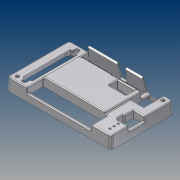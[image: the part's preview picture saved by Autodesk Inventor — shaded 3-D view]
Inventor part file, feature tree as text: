
AUTODESK INVENTOR PART (.ipt)
format: ipt  version: unknown  size: 2,817,024 bytes
history: native  units: mm (DEFAULTED — no unit token found)
features: extrude x22, sketch x13, fillet x7, plane x7, other x6, projected_geometry x1
ambient origin geometry x5: Origin, X Axis, Y Axis, Z Axis, Center Point
feature tree (56):
  other  "Basic Profile Sketch"
  extrude  "Above PCB Extrusion"  Depth=71.12mm
  extrude  "Below Extrusion"  Depth=10.16mm
  extrude  "Board Level Edge Cuts"  Depth=2.032mm
  extrude  "Board Level Supports"  Depth=48.1076mm
  extrude  "LED Viewing Angle Increase"  Depth=8.382mm
  other  "DB Sketch"
  extrude  "Side Reliefs"  Depth=4.318mm
  fillet  "Fillet2"  Radius=3.81mm
  extrude  "Board Level Cut"  Depth=25.4mm
  other  "Snap Edge Draft"
  plane  "Work Plane3"
  plane  "Work Plane4"
  plane  "Work Plane5"
  plane  "Work Plane7"
  other  "Snap Sketch"
  extrude  "Relay Snap"  Depth=3.81mm
  extrude  "Relay Snap Cut"  Depth=3.175mm
  extrude  "DIO Snap"  Depth=8.89mm
  extrude  "DIO Snap Cut"  Depth=3.81mm
  extrude  "DIO Snap Cut 2"  Depth=2.032mm
  extrude  "DB Cut"  Depth=3.81mm
  extrude  "Mounting Holes"  Depth=6.35mm
  extrude  "LED, Power, and BFL Holes"  Depth=2.3114mm
  extrude  "I2C Clearance"  Depth=1.27mm
  extrude  "I2C Top Clearance"  Depth=25.4mm
  extrude  "Screw Bosses"  Depth=1.27mm
  other  "Ribs"
  extrude  "Bottom Clearance Cut"  Depth=6.35mm
  other  "Troublesome Components Sketch"
  extrude  "TC Cut 1"  Depth=7.62mm
  extrude  "TC Cut 2"  Depth=35.56mm
  extrude  "TC Cut 3"  Depth=20.32mm
  fillet  "Top Fillets 1"  Radius=5.08mm
  fillet  "Top Fillets 2"  Radius=2.54mm
  fillet  "Rib and Wall Intersection Fillets"  Radius=1.27mm
  fillet  "Bottom Fillets 1"  Radius=25.4mm
  fillet  "Bottom Fillets 2"  Radius=10.16mm
  fillet  "Bottom Fillets 3"  Radius=13.97mm
  plane  "YZ Plane (RIGHT)"
  plane  "XZ Plane (TOP)"
  plane  "XY Plane (FRONT)"
  sketch  "Sketch3"  dims[d0=121.92mm d1=71.12mm]
  sketch  "Sketch9"  dims[d2=2.54mm d3=10.16mm d4=-0.523599mm]
  sketch  "Sketch13"  dims[d5=6.35mm d6=0.523599mm d7=2.032mm]
  sketch  "Sketch14"  dims[d8=10.922mm d9=-0.523599mm]
  sketch  "Sketch15"  dims[d10=14.074mm d11=63.5mm d12=70.844mm d13=5.6261mm d14=63.5mm d15=10.16mm d16=1.016mm d17=1.016mm d18=0.79375mm d19=55.195489mm d20=0.79375mm d21=58.06186mm d22=1.745329mm d24=48.1076mm]
  sketch  "Sketch16"  dims[d27=4.064mm d28=0.523599mm d42=8.382mm d43=-0.523599mm]
  sketch  "Sketch17"  dims[d54=1.22173mm d65=4.318mm d70=3.81mm]
  sketch  "Sketch18"  dims[d71=3.81mm d72=25.4mm d73=0.523599mm]
  sketch  "Sketch20"  dims[d78=3.81mm d79=3.81mm]
  sketch  "Sketch23"  dims[d80=6.35mm d81=3.175mm]
  sketch  "Sketch24"  dims[d82=8.128mm d83=-0.523599mm d84=8.89mm d85=0.349066mm]
  projected_geometry  "Projected Loop2"
  sketch  "Sketch27"  dims[d86=3.81mm d87=3.81mm]
  sketch  "Sketch28"  dims[d88=5.3848mm d89=2.032mm d90=-0.523599mm d94=3.81mm d95=6.35mm d96=2.3114mm d99=1.27mm d100=25.4mm d101=0.174533mm d102=1.27mm d103=2.54mm d104=0.174533mm d105=6.35mm d107=7.62mm d108=35.56mm d109=20.32mm d110=5.08mm d111=2.54mm d112=1.27mm d113=25.4mm d114=10.16mm d116=13.97mm d117=20.32mm d118=2.032mm d119=1.016mm d120=0.762mm d121=2.032mm d123=2.032mm d124=1.016mm d125=1.016mm d126=1.016mm d127=74.93mm d128=15.24mm d129=1.27mm d130=23.495mm d131=1.905mm d132=1.905mm d133=1.016mm d134=5.08mm d135=5.08mm d136=2.54mm d137=6.35mm d138=5.08mm d143=7.62mm d144=0.0mm d146=25.4mm d147=0.0mm d148=0.523599mm d151=25.4mm d152=0.0mm d153=25.4mm d154=0.0mm d155=1.905mm d156=0.523599mm d157=1.27mm d158=7.62mm d159=2.54mm d160=2.54mm d161=2.54mm d162=1.143mm d163=1.016mm d164=0.508mm d166=6.35mm d167=1.27mm d168=0.79375mm d170=45.0deg d172=10.922mm d173=0.762mm d174=38.354mm d175=19.7612mm d176=0.762mm d177=0.762mm d178=5.08mm d179=2.2098mm d180=1.016mm d184=0.762mm d185=2.032mm d186=1.016mm d188=1.396263mm d189=0.872665mm d190=25.4mm d191=0.0mm d194=10.668mm d200=30.0deg d201=1.651mm d202=25.4mm d203=0.0mm d204=18.161mm d206=0.212985mm d208=2.286mm d209=-0.523599mm d213=75.565mm d216=35.56mm d220=1.524mm d221=5.842mm d222=2.54mm d223=2.54mm d224=1.016mm d225=-0.872665mm d226=-0.872665mm d227=-0.872665mm d228=-0.872665mm d231=3.048mm d232=1.016mm d233=1.016mm d237=7.5946mm d238=7.5946mm d239=0.9906mm d240=-0.523599mm d241=20.4724mm d242=4.0132mm d243=4.6482mm d252=23.4442mm d253=4.6736mm d254=16.256mm d255=10.668mm d256=3.6576mm d257=-0.523599mm d258=1.016mm d259=2.032mm d260=0.396875mm d261=0.127mm d262=1.016mm d263=0.396875mm d265=0.508mm d266=0.396875mm d267=0.396875mm d269=14.478mm d270=17.453293mm d271=105.41mm d272=55.88mm d273=26.67mm d274=115.57mm d275=1.524mm d277=47.625mm d278=48.26mm d279=1.143mm d280=5.08mm d281=0.508mm d282=0.508mm d283=7.112mm d284=1.778mm d285=4.8514mm d286=105.41mm d287=0.254mm d288=25.4mm d289=0.523599mm d290=1.016mm d291=1.016mm d292=30.7848mm d293=12.6238mm d294=10.0076mm d295=2.794mm d296=12.7254mm d297=8.2042mm d298=8.0772mm d299=1.524mm d300=1.524mm d301=1.3208mm d302=0.0mm d303=0.254mm d304=1.524mm d305=1.905mm d306=3.048mm d307=1.016mm d308=0.396875mm d309=0.396875mm d310=1.016mm d311=0.508mm d312=0.127mm d313=0.508mm d314=-0.523599mm]
